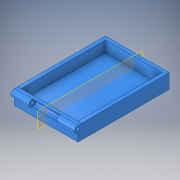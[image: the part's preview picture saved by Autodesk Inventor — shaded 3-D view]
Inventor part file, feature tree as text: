
AUTODESK INVENTOR PART (.ipt)
format: ipt  version: 2017 SP1 (Build 210196100, 196)  size: 176,640 bytes
history: native  units: in
note: dims shown in document units (in); Inventor stores cm internally (conversion verified against a paired STEP export)
features: extrude x7, sketch x7, plane x1
ambient origin geometry x8: Origin, YZ Plane, XZ Plane, XY Plane, X Axis, Y Axis, Z Axis, Center Point
bodies: Solid1 (feature_tree)
feature tree (15):
  extrude  "Extrusion1"  Depth=3.0in
  extrude  "Extrusion2"  TaperAngle=0.0deg  [1 undecoded]
  extrude  "Extrusion5"  Depth=3.3125in
  extrude  "Extrusion6"  TaperAngle=0.0deg  [1 undecoded]
  extrude  "Extrusion9"  Depth=0.125in
  extrude  "Extrusion10"  TaperAngle=0.0deg  [1 undecoded]
  plane  "Work Plane1"
  extrude  "Extrusion11"  Depth=2.3125in
  sketch  "Sketch2"  dims[d0=2.0in d1=3.0in]
  sketch  "Sketch3"  dims[d2=0.5625in d3=0.0in]
  sketch  "Sketch6"  dims[d4=2.3125in d5=3.3125in]
  sketch  "Sketch8"  dims[d6=0.125in d7=0.0in]
  sketch  "Sketch11"  dims[d8=0.125in d9=0.125in]
  sketch  "Sketch12"  dims[d10=0.2812in d11=0.0in]
  sketch  "Sketch13"  dims[d16=0.25in d19=2.3125in d20=0.0in d21=0.125in d22=2.3125in d23=0.0in d28=0.125in d29=0.0in d30=2.3125in d31=0.0in d32=-1.1565in d33=0.25in d34=1.0in d35=0.0in]
note: 3 required parameter values undecoded (feature->parameter linkage not recoverable at this tier; creation-order binding heuristic only, values carry confidence <= 0.55)
